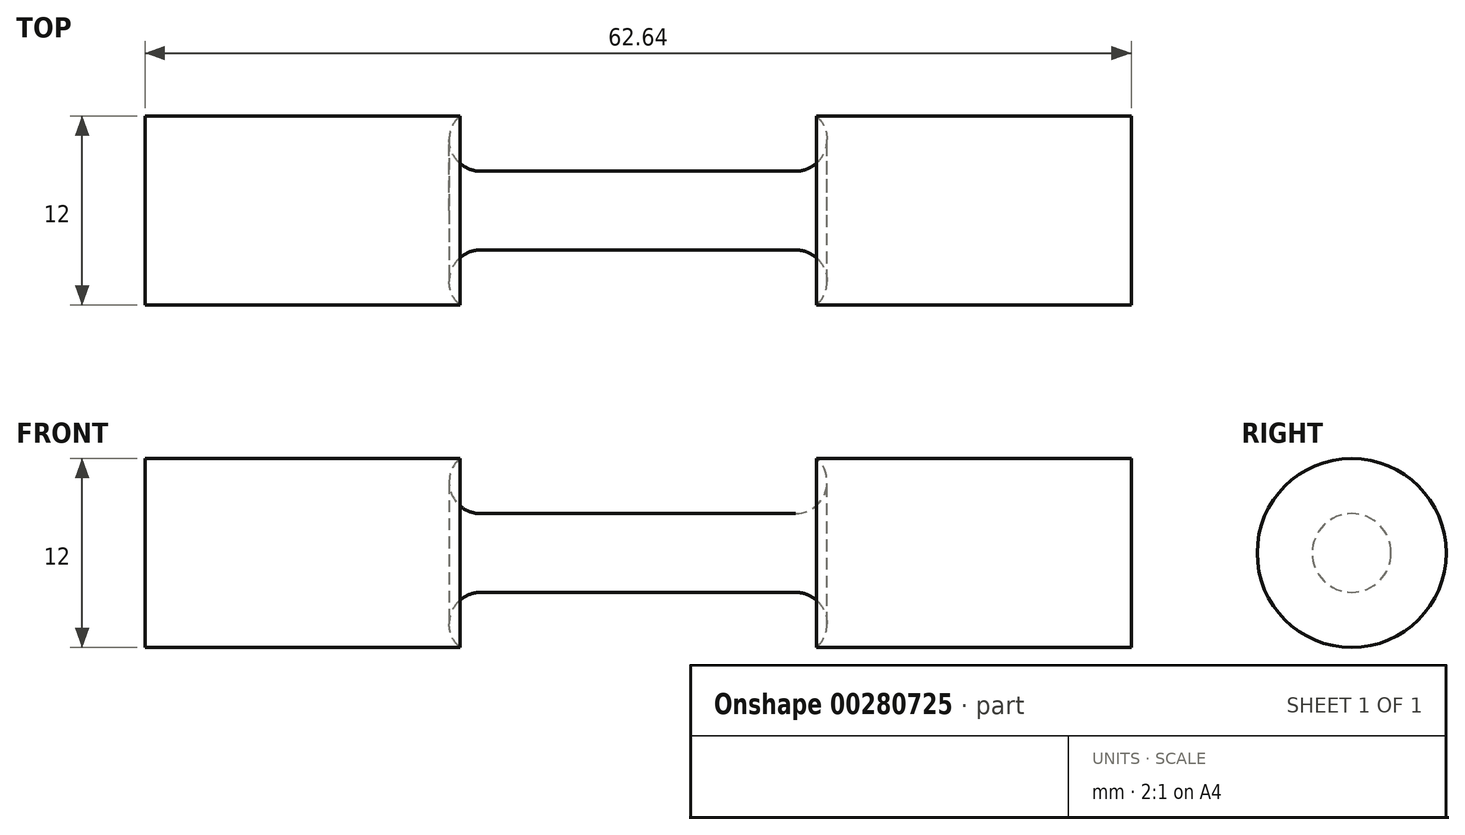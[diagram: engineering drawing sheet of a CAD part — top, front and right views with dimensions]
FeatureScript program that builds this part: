
annotation { "Feature Type Name" : "Feature", "Feature Type Description" : "" }
export const myFeature = defineFeature(function(context is Context, id is Id, definition is map)
    precondition{}
    {
        {
            var Q0;
            Q0=qCreatedBy(makeId("Front.planeOp"),FACE);
            var sketch = newSketch(context, id + "F0", { "sketchPlane" : qUnion([Q0])});
            skLineSegment(sketch, "E0", {"start": v(0, 2.5) * mm, "end": v(10, 2.5) * mm});
            skArc(sketch, "E1", {"start": v(10, 2.5) * mm, "mid": v(11.87, 3.8) * mm, "end": v(11.32, 6) * mm});
            skLineSegment(sketch, "E2", {"start": v(11.32, 6) * mm, "end": v(31.32, 6) * mm});
            skLineSegment(sketch, "E3", {"start": v(31.32, 6) * mm, "end": v(31.32, 0) * mm});
            skLineSegment(sketch, "E4.MirrorCS", {"start": v(-31.32, 6) * mm, "end": v(-31.32, 0) * mm});
            skArc(sketch, "E5.MirrorCS", {"start": v(-10, 2.5) * mm, "mid": v(-11.87, 3.8) * mm, "end": v(-11.32, 6) * mm});
            skLineSegment(sketch, "E6.MirrorCS", {"start": v(0, 2.5) * mm, "end": v(-10, 2.5) * mm});
            skLineSegment(sketch, "E7.MirrorCS", {"start": v(-11.32, 6) * mm, "end": v(-31.32, 6) * mm});
            skLineSegment(sketch, "E8", {"start": v(-31.32, 0) * mm, "end": v(31.32, 0) * mm});
            skSolve(sketch);
        }
        {
            var Q0;
            Q0 = qSketchRegion(id + "F0", true);
            var Q1;
            Q1=sQuery(id+"F0.wireOp",EDGE,"E8");
            revolve(context, id + "F1", {"entities" : qUnion([Q0]), "axis" : qUnion([Q1]), "revolveType" : RevolveType.FULL});
        }
    });
